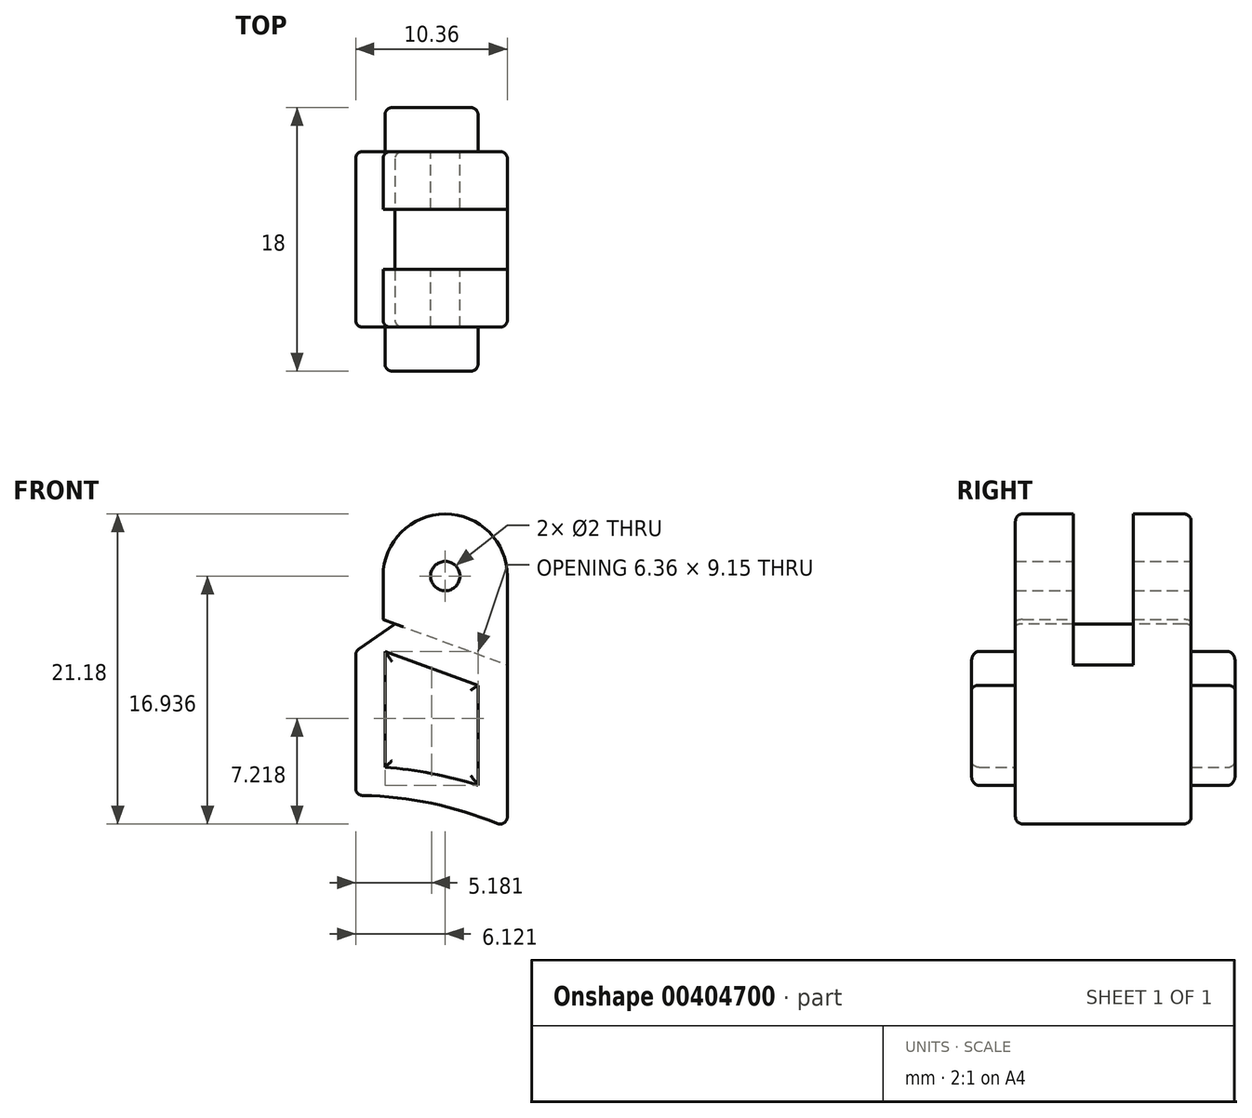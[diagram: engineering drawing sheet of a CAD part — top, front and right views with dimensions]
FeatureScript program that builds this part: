
annotation { "Feature Type Name" : "Feature", "Feature Type Description" : "" }
export const myFeature = defineFeature(function(context is Context, id is Id, definition is map)
    precondition{}
    {
        {
            var Q0;
            Q0=qCreatedBy(makeId("Front.planeOp"),FACE);
            var sketch = newSketch(context, id + "F0", { "sketchPlane" : qUnion([Q0])});
            skLineSegment(sketch, "E0.0", {"start": v(0, 38.1) * mm, "end": v(10.36, 34.33) * mm});
            skLineSegment(sketch, "E1", {"start": v(0, 38.1) * mm, "end": v(0, 25.4) * mm});
            skLineSegment(sketch, "E2.0", {"start": v(10.36, 23.2) * mm, "end": v(10.36, 34.33) * mm});
            skArc(sketch, "E3.trimOffspring", {"start": v(10.36, 23.2) * mm, "mid": v(5.3, 24.84) * mm, "end": v(0, 25.4) * mm});
            skLineSegment(sketch, "E4.0", {"start": v(2, 35.24) * mm, "end": v(2, 27.33) * mm});
            skArc(sketch, "E5.trimOffspring", {"start": v(8.36, 26.1) * mm, "mid": v(5.22, 26.9) * mm, "end": v(2, 27.33) * mm});
            skLineSegment(sketch, "E6.trimOffspring", {"start": v(8.36, 26.1) * mm, "end": v(8.36, 32.93) * mm});
            skLineSegment(sketch, "E7.trimOffspring", {"start": v(2, 35.24) * mm, "end": v(8.36, 32.93) * mm});
            skSolve(sketch);
        }
        {
            var Q0;
            Q0=makeQuery(id+"F0.imprint","IMPRINT",FACE,{"disambiguationData":[TD([[makeQuery(id+"F0.imprint","IMPRINT",EDGE,{"derivedFrom":sQuery(id+"F0.wireOp",EDGE,"E0.0")}),-1.0]])]});
            extrude(context, id + "F1", {"entities" : qUnion([Q0]), "depth" : 12 * mm, "symmetric" : true});
        }
        {
            var Q0;
            Q0=makeQuery(id+"F0.imprint","IMPRINT",FACE,{"disambiguationData":[TD([[makeQuery(id+"F0.imprint","IMPRINT",EDGE,{"derivedFrom":sQuery(id+"F0.wireOp",EDGE,"E4.0")}),1.0]])]});
            extrude(context, id + "F2", {"entities" : qUnion([Q0]), "operationType" : NewBodyOperationType.ADD, "depth" : 18 * mm, "symmetric" : true});
        }
        {
            var Q0;
            Q0=makeQuery(id+"F1.opExtrude","SWEPT_EDGE",EDGE,{"disambiguationData":[OSD([sQuery(id+"F0.wireOp",EDGE,"E0.0"),sQuery(id+"F0.wireOp",EDGE,"E1")])]});
            chamfer(context, id + "F3", {"entities" : qUnion([Q0]), "width" : 2 * mm, "tangentPropagation" : true});
        }
        {
            var Q0;
            Q0=qCreatedBy(makeId("Front.planeOp"),FACE);
            var sketch = newSketch(context, id + "F4", { "sketchPlane" : qUnion([Q0])});
            skLineSegment(sketch, "E8.0", {"start": v(1.88, 37.42) * mm, "end": v(10.36, 34.33) * mm});
            skLineSegment(sketch, "E9", {"start": v(1.88, 37.42) * mm, "end": v(1.88, 40.39) * mm});
            skLineSegment(sketch, "E10", {"start": v(10.36, 34.33) * mm, "end": v(10.36, 40.39) * mm});
            skArc(sketch, "E11", {"start": v(10.36, 40.39) * mm, "mid": v(6.12, 44.63) * mm, "end": v(1.88, 40.39) * mm});
            skCircle(sketch, "E12", {"center": v(6.12, 40.39) * mm, "radius": 1 * mm});
            skSolve(sketch);
        }
        {
            var Q0;
            Q0 = qSketchRegion(id + "F4", true);
            extrude(context, id + "F5", {"entities" : qUnion([Q0]), "operationType" : NewBodyOperationType.ADD, "depth" : 12 * mm, "symmetric" : true});
        }
        {
            var Q0;
            Q0 = qSketchRegion(id + "F4", true);
            extrude(context, id + "F6", {"entities" : qUnion([Q0]), "operationType" : NewBodyOperationType.REMOVE, "depth" : 4.1 * mm, "symmetric" : true});
        }
        {
            var Q0;
            Q0=makeQuery(id+"F1.opExtrude","SWEPT_EDGE",EDGE,{"disambiguationData":[OSD([sQuery(id+"F0.wireOp",EDGE,"E1"),sQuery(id+"F0.wireOp",EDGE,"E3.trimOffspring")])]});
            var Q1;
            {var subQ0=sQuery(id+"F0.wireOp",EDGE,"E1");Q1=makeQuery(id+"F3.opChamfer","BLEND_EDGE",EDGE,{"blendedFrom":[makeQuery(id+"F1.opExtrude","SWEPT_EDGE",EDGE,{"disambiguationData":[OSD([sQuery(id+"F0.wireOp",EDGE,"E0.0"),subQ0])]}),makeQuery(id+"F1.opExtrude","SWEPT_FACE",FACE,{"disambiguationData":[OSD([subQ0])]})],"blendedInto":[makeQuery(id+"F1.opExtrude","SWEPT_FACE",FACE,{"disambiguationData":[OSD([subQ0])]})]});}
            var Q2;
            Q2=makeQuery(id+"F1.opExtrude","SWEPT_EDGE",EDGE,{"disambiguationData":[OSD([sQuery(id+"F0.wireOp",EDGE,"E2.0"),sQuery(id+"F0.wireOp",EDGE,"E3.trimOffspring")])]});
            var Q3;
            Q3=makeQuery(id+"F5.boolean.opBoolean","MERGE",EDGE,{"derivedFrom":[makeQuery(id+"F1.opExtrude","CAP_EDGE",EDGE,{"disambiguationData":[OSD([sQuery(id+"F0.wireOp",EDGE,"E2.0")])],"isStart":true}),makeQuery(id+"F5.opExtrude","CAP_EDGE",EDGE,{"disambiguationData":[OSD([sQuery(id+"F4.wireOp",EDGE,"E10")])],"isStart":true})]});
            var Q4;
            Q4=makeQuery(id+"F1.opExtrude","CAP_EDGE",EDGE,{"disambiguationData":[OSD([sQuery(id+"F0.wireOp",EDGE,"E1")])],"isStart":true});
            var Q5;
            Q5=makeQuery(id+"F1.opExtrude","CAP_EDGE",EDGE,{"disambiguationData":[OSD([sQuery(id+"F0.wireOp",EDGE,"E1")])],"isStart":false});
            var Q6;
            Q6=makeQuery(id+"F5.opExtrude","CAP_EDGE",EDGE,{"disambiguationData":[OSD([sQuery(id+"F4.wireOp",EDGE,"E11")])],"isStart":false});
            var Q7;
            {var subQ0=sQuery(id+"F0.wireOp",EDGE,"E1");var subQ1=sQuery(id+"F0.wireOp",EDGE,"E0.0");Q7=makeQuery(id+"F3.opChamfer","BLEND_EDGE",EDGE,{"blendedFrom":[makeQuery(id+"F1.opExtrude","SWEPT_EDGE",EDGE,{"disambiguationData":[OSD([subQ1,subQ0])]}),makeQuery(id+"F1.opExtrude","CAP_FACE",FACE,{"disambiguationData":[OSD([subQ1,subQ0,sQuery(id+"F0.wireOp",EDGE,"E2.0"),sQuery(id+"F0.wireOp",EDGE,"E3.trimOffspring"),sQuery(id+"F0.wireOp",EDGE,"E4.0"),sQuery(id+"F0.wireOp",EDGE,"E5.trimOffspring"),sQuery(id+"F0.wireOp",EDGE,"E6.trimOffspring"),sQuery(id+"F0.wireOp",EDGE,"E7.trimOffspring")])],"isStart":false})],"blendedInto":[makeQuery(id+"F1.opExtrude","CAP_FACE",FACE,{"disambiguationData":[OSD([subQ1,subQ0,sQuery(id+"F0.wireOp",EDGE,"E2.0"),sQuery(id+"F0.wireOp",EDGE,"E3.trimOffspring"),sQuery(id+"F0.wireOp",EDGE,"E4.0"),sQuery(id+"F0.wireOp",EDGE,"E5.trimOffspring"),sQuery(id+"F0.wireOp",EDGE,"E6.trimOffspring"),sQuery(id+"F0.wireOp",EDGE,"E7.trimOffspring")])],"isStart":false})]});}
            var Q8;
            {var subQ0=sQuery(id+"F0.wireOp",EDGE,"E1");var subQ1=sQuery(id+"F0.wireOp",EDGE,"E0.0");Q8=makeQuery(id+"F3.opChamfer","BLEND_EDGE",EDGE,{"blendedFrom":[makeQuery(id+"F1.opExtrude","SWEPT_EDGE",EDGE,{"disambiguationData":[OSD([subQ1,subQ0])]}),makeQuery(id+"F1.opExtrude","CAP_FACE",FACE,{"disambiguationData":[OSD([subQ1,subQ0,sQuery(id+"F0.wireOp",EDGE,"E2.0"),sQuery(id+"F0.wireOp",EDGE,"E3.trimOffspring"),sQuery(id+"F0.wireOp",EDGE,"E4.0"),sQuery(id+"F0.wireOp",EDGE,"E5.trimOffspring"),sQuery(id+"F0.wireOp",EDGE,"E6.trimOffspring"),sQuery(id+"F0.wireOp",EDGE,"E7.trimOffspring")])],"isStart":true})],"blendedInto":[makeQuery(id+"F1.opExtrude","CAP_FACE",FACE,{"disambiguationData":[OSD([subQ1,subQ0,sQuery(id+"F0.wireOp",EDGE,"E2.0"),sQuery(id+"F0.wireOp",EDGE,"E3.trimOffspring"),sQuery(id+"F0.wireOp",EDGE,"E4.0"),sQuery(id+"F0.wireOp",EDGE,"E5.trimOffspring"),sQuery(id+"F0.wireOp",EDGE,"E6.trimOffspring"),sQuery(id+"F0.wireOp",EDGE,"E7.trimOffspring")])],"isStart":true})]});}
            var Q9;
            Q9=makeQuery(id+"F2.opExtrude","CAP_FACE",FACE,{"disambiguationData":[OSD([sQuery(id+"F0.wireOp",EDGE,"E4.0"),sQuery(id+"F0.wireOp",EDGE,"E5.trimOffspring"),sQuery(id+"F0.wireOp",EDGE,"E6.trimOffspring"),sQuery(id+"F0.wireOp",EDGE,"E7.trimOffspring")])],"isStart":true});
            var Q10;
            Q10=makeQuery(id+"F1.opExtrude","CAP_EDGE",EDGE,{"disambiguationData":[OSD([sQuery(id+"F0.wireOp",EDGE,"E7.trimOffspring")])],"isStart":true});
            var Q11;
            Q11=makeQuery(id+"F1.opExtrude","CAP_EDGE",EDGE,{"disambiguationData":[OSD([sQuery(id+"F0.wireOp",EDGE,"E6.trimOffspring")])],"isStart":true});
            var Q12;
            Q12=makeQuery(id+"F1.opExtrude","CAP_EDGE",EDGE,{"disambiguationData":[OSD([sQuery(id+"F0.wireOp",EDGE,"E5.trimOffspring")])],"isStart":true});
            var Q13;
            Q13=makeQuery(id+"F1.opExtrude","CAP_EDGE",EDGE,{"disambiguationData":[OSD([sQuery(id+"F0.wireOp",EDGE,"E4.0")])],"isStart":true});
            var Q14;
            Q14=makeQuery(id+"F2.opExtrude","CAP_FACE",FACE,{"disambiguationData":[OSD([sQuery(id+"F0.wireOp",EDGE,"E4.0"),sQuery(id+"F0.wireOp",EDGE,"E5.trimOffspring"),sQuery(id+"F0.wireOp",EDGE,"E6.trimOffspring"),sQuery(id+"F0.wireOp",EDGE,"E7.trimOffspring")])],"isStart":false});
            var Q15;
            Q15=makeQuery(id+"F1.opExtrude","CAP_EDGE",EDGE,{"disambiguationData":[OSD([sQuery(id+"F0.wireOp",EDGE,"E7.trimOffspring")])],"isStart":false});
            var Q16;
            Q16=makeQuery(id+"F1.opExtrude","CAP_EDGE",EDGE,{"disambiguationData":[OSD([sQuery(id+"F0.wireOp",EDGE,"E4.0")])],"isStart":false});
            var Q17;
            Q17=makeQuery(id+"F1.opExtrude","CAP_EDGE",EDGE,{"disambiguationData":[OSD([sQuery(id+"F0.wireOp",EDGE,"E5.trimOffspring")])],"isStart":false});
            var Q18;
            Q18=makeQuery(id+"F1.opExtrude","CAP_EDGE",EDGE,{"disambiguationData":[OSD([sQuery(id+"F0.wireOp",EDGE,"E6.trimOffspring")])],"isStart":false});
            var Q19;
            Q19=makeQuery(id+"F1.opExtrude","CAP_EDGE",EDGE,{"disambiguationData":[OSD([sQuery(id+"F0.wireOp",EDGE,"E3.trimOffspring")])],"isStart":false});
            var Q20;
            Q20=makeQuery(id+"F1.opExtrude","CAP_EDGE",EDGE,{"disambiguationData":[OSD([sQuery(id+"F0.wireOp",EDGE,"E3.trimOffspring")])],"isStart":true});
            var Q21;
            Q21=makeQuery(id+"F6.boolean.opBoolean","COPY",EDGE,{"derivedFrom":makeQuery(id+"F6.opExtrude","CAP_EDGE",EDGE,{"disambiguationData":[OSD([sQuery(id+"F4.wireOp",EDGE,"E11")])],"isStart":true})});
            var Q22;
            Q22=makeQuery(id+"F6.boolean.opBoolean","COPY",EDGE,{"derivedFrom":makeQuery(id+"F6.opExtrude","CAP_EDGE",EDGE,{"disambiguationData":[OSD([sQuery(id+"F4.wireOp",EDGE,"E11")])],"isStart":false})});
            var Q23;
            Q23=makeQuery(id+"F6.boolean.opBoolean","COPY",EDGE,{"derivedFrom":makeQuery(id+"F6.opExtrude","SWEPT_EDGE",EDGE,{"disambiguationData":[OSD([sQuery(id+"F4.wireOp",EDGE,"E8.0"),sQuery(id+"F4.wireOp",EDGE,"E10")])]})});
            fillet(context, id + "F7", {"entities" : qUnion([Q0, Q1, Q2, Q3, Q4, Q5, Q6, Q7, Q8, Q9, Q10, Q11, Q12, Q13, Q14, Q15, Q16, Q17, Q18, Q19, Q20, Q21, Q22, Q23]), "radius" : .5 * mm, "tangentPropagation" : true, "allowEdgeOverflow" : false});
        }
    });
